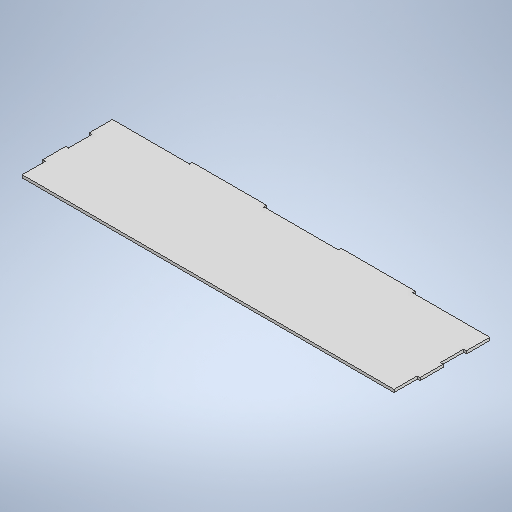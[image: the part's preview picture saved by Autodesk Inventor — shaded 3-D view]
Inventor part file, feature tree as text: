
AUTODESK INVENTOR PART (.ipt)
format: ipt  version: 2025.1 (Build 291241020, 241B)  size: 259,072 bytes
history: native  units: mm
features: extrude x1, sketch x1
ambient origin geometry x8: Origin, YZ Plane, XZ Plane, XY Plane, X Axis, Y Axis, Z Axis, Center Point
bodies: Solid1 (feature_tree)
feature tree (2):
  extrude  "Extrusion1"  Depth=100.0mm
  sketch  "Sketch1"  dims[d0=400.0mm d1=100.0mm d7=3.0mm d8=80.0mm d11=25.0mm d12=3.0mm d14=3.0mm d15=0.0mm]
